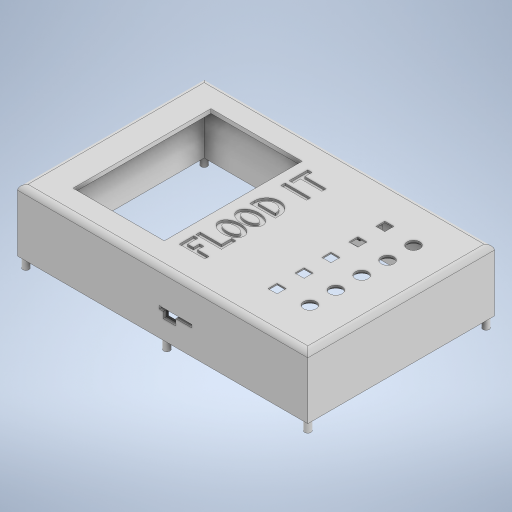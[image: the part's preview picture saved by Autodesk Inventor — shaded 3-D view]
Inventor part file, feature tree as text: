
AUTODESK INVENTOR PART (.ipt)
format: ipt  version: 2023 (Build 270158000, 158)  size: 708,608 bytes
history: native  units: in
note: dims shown in document units (in); Inventor stores cm internally (conversion verified against a paired STEP export)
features: extrude x16, sketch x14, fillet x2
ambient origin geometry x8: Origin, YZ Plane, XZ Plane, XY Plane, X Axis, Y Axis, Z Axis, Center Point
bodies: Solid1 (feature_tree)
feature tree (32):
  extrude  "Extrusion1"  Depth=4.5in
  extrude  "Extrusion2"  Depth=0.2in
  fillet  "Fillet1"  Radius=1.4in
  extrude  "Extrusion3"  Depth=0.125in
  extrude  "Extrusion4"  Depth=2.2in
  extrude  "Extrusion5"  Depth=0.5875in
  sketch  "Sketch6"  dims[d13=0.75in d14=1.4in d15=0.0in]
  extrude  "Extrusion6"  Depth=1.4in TaperAngle=0.0deg
  extrude  "Extrusion9"  Depth=0.1in
  extrude  "Extrusion10"  Depth=0.1in
  extrude  "Extrusion11"  Depth=0.25in
  extrude  "Extrusion12"  Depth=0.15in
  extrude  "Extrusion13"  Depth=0.7in
  extrude  "Extrusion14"  Depth=0.1in
  extrude  "Extrusion15"  Depth=0.615in
  extrude  "Extrusion16"  Depth=0.0625in
  fillet  "Fillet2"  Radius=0.21in
  extrude  "Extrusion18"  Depth=0.0625in
  extrude  "Extrusion19"  Depth=0.0625in
  sketch  "Sketch1"  dims[d0=7.0in d1=4.5in]
  sketch  "Sketch2"  dims[d2=1.5in d3=0.0in d4=0.2in d5=1.4in d6=0.0in]
  sketch  "Sketch3"  dims[d7=0.125in d8=0.25in]
  sketch  "Sketch4"  dims[d9=0.25in d10=2.2in]
  sketch  "Sketch5"  dims[d11=3.325in d12=0.5875in]
  sketch  "Sketch8"  dims[d16=0.1in d17=0.14in]
  sketch  "Sketch9"  dims[d18=0.1in d19=0.275in]
  sketch  "Sketch10"  dims[d20=0.35in d21=0.25in]
  sketch  "Sketch11"  dims[d22=0.15in d23=0.15in]
  sketch  "Sketch12"  dims[d24=0.25in d25=0.7in]
  sketch  "Sketch13"  dims[d26=0.1in d27=0.1in]
  sketch  "Sketch15"  dims[d28=0.25in d29=0.615in]
  sketch  "Sketch16"  dims[d30=0.25in d31=1.1in d32=0.21in d33=0.3075in d34=0.5575in d35=1.65in d36=0.3075in d37=0.21in d38=0.5575in d39=2.1in d40=0.1in d41=0.1in d42=0.3in d43=0.1in d44=0.25in d45=0.615in d46=2.4in d47=0.11in d48=2.51in d49=0.5575in d50=0.1in d51=0.615in d52=0.175in d53=0.175in d54=0.1in d55=0.1in d56=0.25in d57=3.15in d58=0.1in d59=0.515in d60=0.05in d61=0.0in d62=0.1125in d63=0.1125in d64=0.2175in d65=0.2175in d66=0.2175in d67=0.2175in d68=0.2175in d69=0.2175in d70=0.65in d71=0.65in d72=0.65in d73=0.65in d74=0.8413in d76=2.25in d77=0.3in d78=0.3in d79=0.3in d80=0.3in d81=0.3in d82=0.625in d83=0.625in d84=0.625in d85=0.625in d86=1.0in d87=3.1in d88=3.1in d89=3.1in d90=3.1in d91=3.1in d92=1.0in d93=0.0in d97=0.4in d98=0.4in d99=0.4in d100=0.4in d101=0.4in d102=0.05in d103=0.0in d124=0.0688in d125=0.0in d126=0.25in d127=0.275in d128=0.25in d129=0.25in d130=0.25in d131=2.1in d132=0.2in d134=0.05in d135=0.0in d142=0.0375in d143=0.0in d144=2.0in d145=0.785in d146=0.0725in d147=0.3in d148=0.15in d149=0.1in d150=0.7in d151=0.2in d152=0.0in d153=0.075in d154=0.125in d155=0.0in d156=0.285in d157=2.5in d158=0.49in d159=0.25in d160=0.0in d161=0.49in d162=0.081in d163=0.0in d164=0.45in d177=0.075in d178=0.0in d179=0.125in d187=2.8in d189=0.04in d190=0.04in d191=0.04in d192=0.04in d193=0.04in d194=0.485in d195=0.0938in d197=3.325in d198=0.254in d199=0.1735in d202=0.075in d203=0.125in d204=0.075in d205=0.125in d206=0.1875in d207=0.1875in d208=0.1875in d209=0.65in d210=0.65in d211=0.65in d212=0.125in d213=0.075in d214=0.025in d215=2.0in d216=0.5in d217=0.0in d218=0.0in d219=0.285in d220=0.1425in d221=0.245in d222=0.285in d224=0.8413in d225=0.15in d226=0.15in d227=0.15in d228=0.15in d229=0.15in d230=0.15in d231=0.1in d232=0.1in d233=0.1in d234=0.1in d235=0.1in d236=0.1in d237=0.1in d238=0.1in d239=0.1in d240=0.1in d241=3.5in d242=3.5in d243=0.245in d244=0.0in d245=0.0625in]
